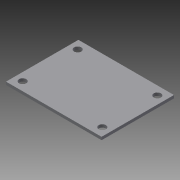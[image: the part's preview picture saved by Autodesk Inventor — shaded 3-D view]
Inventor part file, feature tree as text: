
AUTODESK INVENTOR PART (.ipt)
format: ipt  version: 2014 (Build 180170000, 170)  size: 79,872 bytes
history: native  units: in
note: dims shown in document units (in); Inventor stores cm internally (conversion verified against a paired STEP export)
features: extrude x1, sketch x1
ambient origin geometry x8: Origin, YZ Plane, XZ Plane, XY Plane, X Axis, Y Axis, Z Axis, Center Point
bodies: Solid1 (feature_tree)
feature tree (2):
  extrude  "Extrusion1"  Depth=3.125in
  sketch  "Sketch1"  dims[d0=4.125in d1=3.125in d4=0.3125in d5=0.125in d6=0.0in d7=3.4375in d8=2.375in]
